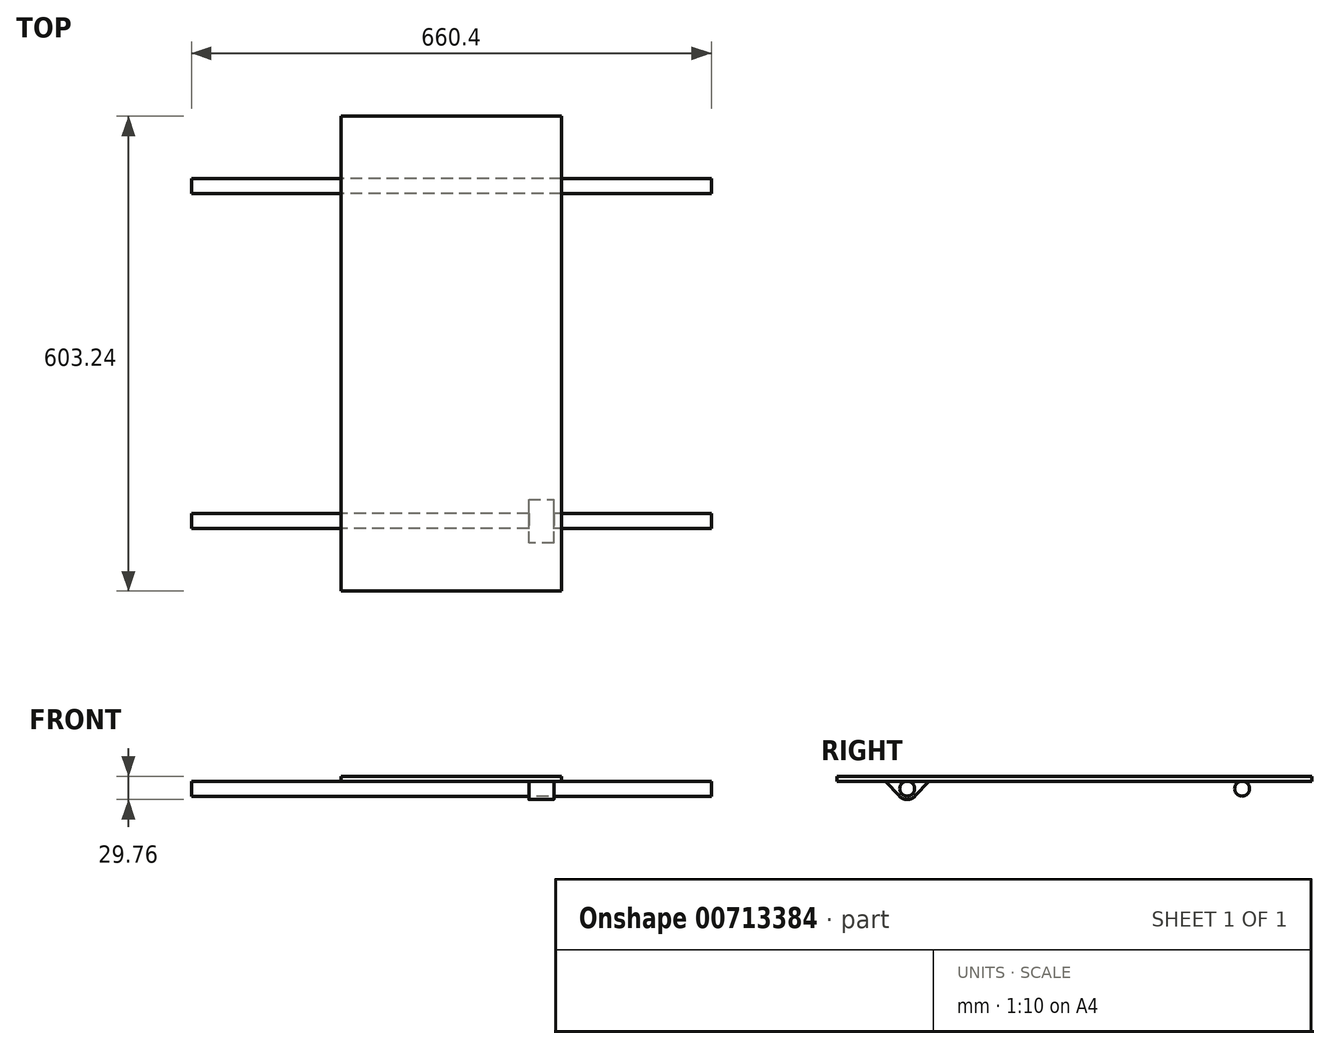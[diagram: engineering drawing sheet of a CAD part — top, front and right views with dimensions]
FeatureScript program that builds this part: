
annotation { "Feature Type Name" : "Feature", "Feature Type Description" : "" }
export const myFeature = defineFeature(function(context is Context, id is Id, definition is map)
    precondition{}
    {
        {
            var Q0;
            Q0=qCreatedBy(makeId("Top.planeOp"),FACE);
            var sketch = newSketch(context, id + "F0", { "sketchPlane" : qUnion([Q0])});
            skLineSegment(sketch, "E0.bottom", {"start": v(139.95, 301.63) * mm, "end": v(-139.95, 301.63) * mm});
            skLineSegment(sketch, "E0.top", {"start": v(139.95, -301.63) * mm, "end": v(-139.95, -301.63) * mm});
            skLineSegment(sketch, "E0.left", {"start": v(139.95, 301.63) * mm, "end": v(139.95, -301.63) * mm});
            skLineSegment(sketch, "E0.right", {"start": v(-139.95, 301.63) * mm, "end": v(-139.95, -301.63) * mm});
            skPoint(sketch, "E0.middle", {"position": v(0, 0) * mm});
            skSolve(sketch);
        }
        {
            var Q0;
            Q0 = qSketchRegion(id + "F0", true);
            extrude(context, id + "F1", {"entities" : qUnion([Q0]), "depth" : 6.35 * mm, "offsetDistance" : 25.4 * mm});
        }
        {
            var Q0;
            Q0=qCreatedBy(makeId("Right.planeOp"),FACE);
            var sketch = newSketch(context, id + "F2", { "sketchPlane" : qUnion([Q0])});
            skLineSegment(sketch, "E1", {"start": v(0, 0) * mm, "end": v(0, -46.08) * mm, "construction": true});
            skCircle(sketch, "E2", {"center": v(-212.73, -9.55) * mm, "radius": 9.53 * mm});
            skCircle(sketch, "E3.MirrorC", {"center": v(212.73, -9.55) * mm, "radius": 9.53 * mm});
            skSolve(sketch);
        }
        {
            var Q0;
            Q0 = qSketchRegion(id + "F2", true);
            extrude(context, id + "F3", {"entities" : qUnion([Q0]), "depth" : 660.4 * mm, "offsetDistance" : 25.4 * mm, "symmetric" : true});
        }
        {
            var Q0;
            Q0=qCreatedBy(makeId("Right.planeOp"),FACE);
            cPlane(context, id + "F4", {"entities" : qUnion([Q0]), "cplaneType" : CPlaneType.OFFSET, "offset" : 98.42 * mm, "width" : 152.4 * mm, "height" : 152.4 * mm});
        }
        {
            var Q0;
            Q0=qCreatedBy(id+"F4.planeOp",FACE);
            var sketch = newSketch(context, id + "F5", { "sketchPlane" : qUnion([Q0])});
            skCircle(sketch, "E4", {"center": v(-212.73, -9.55) * mm, "radius": 13.85 * mm});
            skLineSegment(sketch, "E5", {"start": v(-202.6, -19.01) * mm, "end": v(-178.9, 6.35) * mm});
            skLineSegment(sketch, "E6", {"start": v(-178.9, 6.35) * mm, "end": v(-246.55, 6.35) * mm});
            skLineSegment(sketch, "E7", {"start": v(-246.55, 6.35) * mm, "end": v(-222.85, -19.01) * mm});
            skLineSegment(sketch, "E8", {"start": v(-212.73, -9.55) * mm, "end": v(-212.73, -56.3) * mm, "construction": true});
            skSolve(sketch);
        }
        {
            var Q0;
            Q0 = qSketchRegion(id + "F5", true);
            extrude(context, id + "F6", {"entities" : qUnion([Q0]), "operationType" : NewBodyOperationType.ADD, "depth" : 31.75 * mm, "offsetDistance" : 25.4 * mm});
        }
    });
